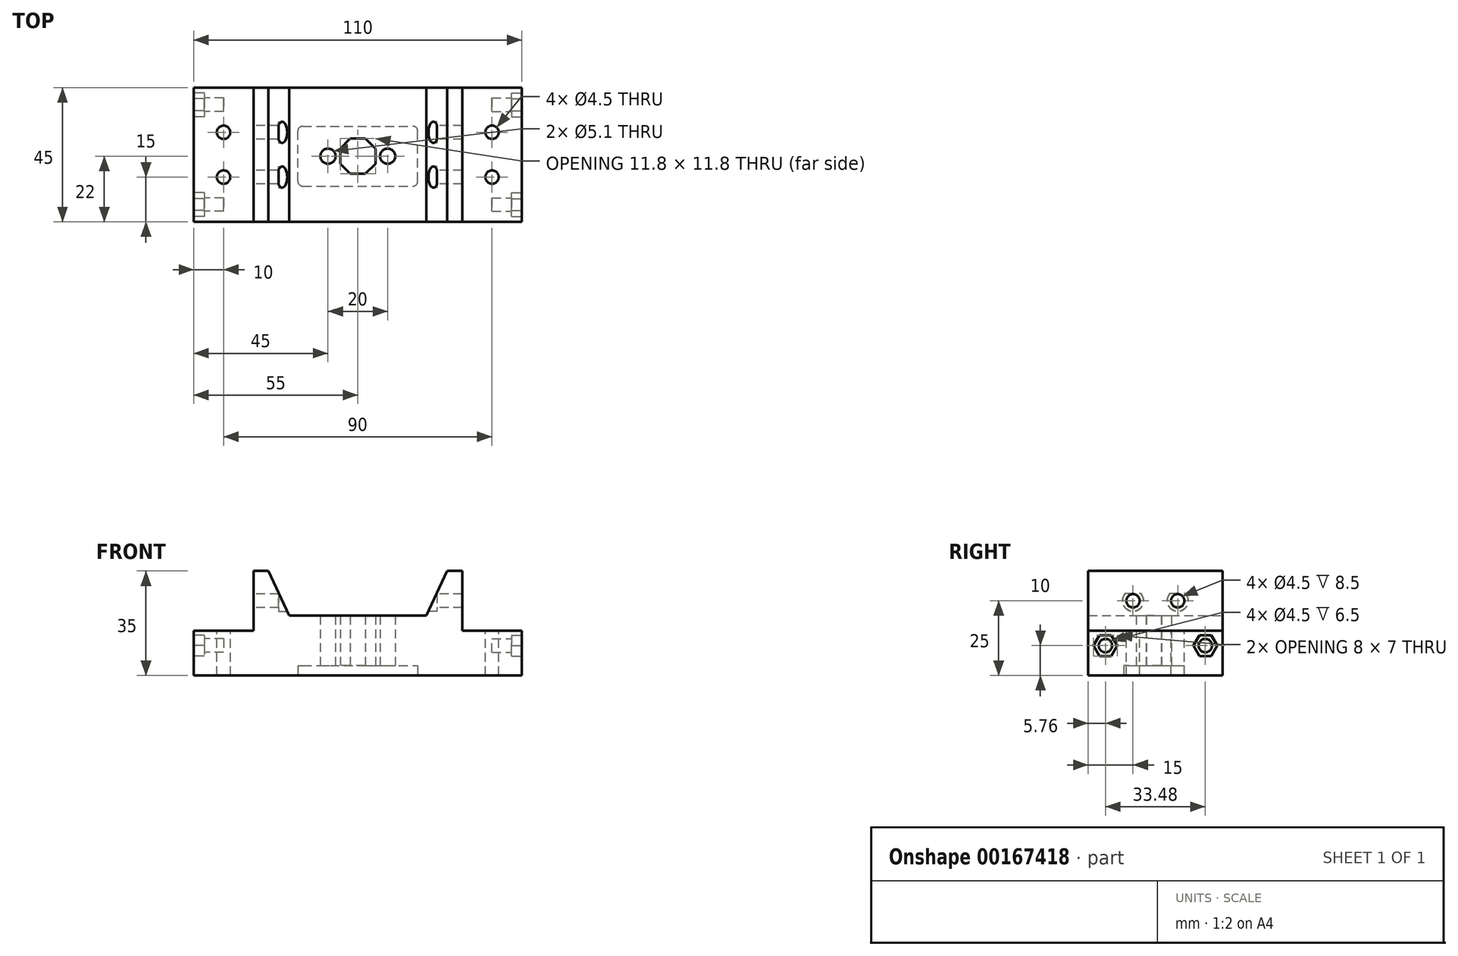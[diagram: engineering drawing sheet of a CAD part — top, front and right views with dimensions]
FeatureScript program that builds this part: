
annotation { "Feature Type Name" : "Feature", "Feature Type Description" : "" }
export const myFeature = defineFeature(function(context is Context, id is Id, definition is map)
    precondition{}
    {
        {
            var Q0;
            Q0=qCreatedBy(makeId("Top.planeOp"),FACE);
            var sketch = newSketch(context, id + "F0", { "sketchPlane" : qUnion([Q0])});
            skLineSegment(sketch, "E0", {"start": v(0, 0) * mm, "end": v(110, 0) * mm});
            skLineSegment(sketch, "E1", {"start": v(110, 0) * mm, "end": v(110, 45) * mm});
            skLineSegment(sketch, "E2", {"start": v(110, 45) * mm, "end": v(0, 45) * mm});
            skLineSegment(sketch, "E3", {"start": v(0, 45) * mm, "end": v(0, 0) * mm});
            skSolve(sketch);
        }
        {
            var Q0;
            Q0 = qSketchRegion(id + "F0", true);
            extrude(context, id + "F1", {"entities" : qUnion([Q0]), "depth" : 15 * mm});
        }
        {
            var Q0;
            Q0=makeQuery(id+"F1.opExtrude","CAP_FACE",FACE,{"disambiguationData":[OSD([sQuery(id+"F0.wireOp",EDGE,"E0"),sQuery(id+"F0.wireOp",EDGE,"E1"),sQuery(id+"F0.wireOp",EDGE,"E2"),sQuery(id+"F0.wireOp",EDGE,"E3")])],"isStart":false});
            var sketch = newSketch(context, id + "F2", { "sketchPlane" : qUnion([Q0])});
            skLineSegment(sketch, "E4", {"start": v(0, 22.5) * mm, "end": v(20, 22.5) * mm, "construction": true});
            skLineSegment(sketch, "E5", {"start": v(110, 22.5) * mm, "end": v(90, 22.5) * mm, "construction": true});
            skLineSegment(sketch, "E6", {"start": v(20, 45) * mm, "end": v(20, 0) * mm});
            skLineSegment(sketch, "E7", {"start": v(20, 0) * mm, "end": v(32, 0) * mm});
            skLineSegment(sketch, "E8", {"start": v(32, 0) * mm, "end": v(32, 45) * mm});
            skLineSegment(sketch, "E9", {"start": v(32, 45) * mm, "end": v(20, 45) * mm});
            skLineSegment(sketch, "E10", {"start": v(90, 45) * mm, "end": v(90, 0) * mm});
            skLineSegment(sketch, "E11", {"start": v(90, 0) * mm, "end": v(78, 0) * mm});
            skLineSegment(sketch, "E12", {"start": v(78, 0) * mm, "end": v(78, 45) * mm});
            skLineSegment(sketch, "E13", {"start": v(78, 45) * mm, "end": v(90, 45) * mm});
            skSolve(sketch);
        }
        {
            var Q0;
            Q0 = qSketchRegion(id + "F2", true);
            extrude(context, id + "F3", {"entities" : qUnion([Q0]), "operationType" : NewBodyOperationType.ADD, "depth" : 20 * mm});
        }
        {
            var Q0;
            Q0=qCreatedBy(makeId("Right.planeOp"),FACE);
            var sketch = newSketch(context, id + "F4", { "sketchPlane" : qUnion([Q0])});
            skCircle(sketch, "E14", {"center": v(15, 25) * mm, "radius": 2.25 * mm});
            skCircle(sketch, "E15", {"center": v(30, 25) * mm, "radius": 2.25 * mm});
            skSolve(sketch);
        }
        {
            var Q0;
            Q0 = qSketchRegion(id + "F4", true);
            var Q1;
            Q1=sQuery(id+"F4.wireOp",EDGE,"E14");
            var Q2;
            Q2=sQuery(id+"F4.wireOp",EDGE,"E15");
            extrude(context, id + "F5", {"entities" : qUnion([Q0]), "operationType" : NewBodyOperationType.REMOVE, "surfaceEntities" : qUnion([Q1, Q2]), "endBound" : BoundingType.THROUGH_ALL, "depth" : 25 * mm});
        }
        {
            var Q0;
            {var subQ0=sQuery(id+"F0.wireOp",EDGE,"E3");var subQ1=sQuery(id+"F0.wireOp",EDGE,"E2");var subQ2=sQuery(id+"F0.wireOp",EDGE,"E0");Q0=makeQuery(id+"F3.boolean.opBoolean","SPLIT",FACE,{"disambiguationData":[TD([makeQuery(id+"F1.opExtrude","SWEPT_FACE",FACE,{"disambiguationData":[OSD([subQ0])]})])],"derivedFrom":makeQuery(id+"F1.opExtrude","CAP_FACE",FACE,{"disambiguationData":[OSD([subQ2,sQuery(id+"F0.wireOp",EDGE,"E1"),subQ1,subQ0])],"isStart":false})});}
            var sketch = newSketch(context, id + "F6", { "sketchPlane" : qUnion([Q0])});
            skCircle(sketch, "E16", {"center": v(10, 30) * mm, "radius": 2.25 * mm});
            skCircle(sketch, "E17", {"center": v(10, 15) * mm, "radius": 2.25 * mm});
            skSolve(sketch);
        }
        {
            var Q0;
            Q0 = qSketchRegion(id + "F6", true);
            extrude(context, id + "F7", {"entities" : qUnion([Q0]), "operationType" : NewBodyOperationType.REMOVE, "endBound" : BoundingType.THROUGH_ALL, "oppositeDirection" : true, "depth" : 25 * mm});
        }
        {
            var Q0;
            {var subQ0=sQuery(id+"F0.wireOp",EDGE,"E2");var subQ1=sQuery(id+"F0.wireOp",EDGE,"E1");var subQ2=sQuery(id+"F0.wireOp",EDGE,"E0");Q0=makeQuery(id+"F3.boolean.opBoolean","SPLIT",FACE,{"disambiguationData":[TD([makeQuery(id+"F1.opExtrude","SWEPT_FACE",FACE,{"disambiguationData":[OSD([subQ1])]})])],"derivedFrom":makeQuery(id+"F1.opExtrude","CAP_FACE",FACE,{"disambiguationData":[OSD([subQ2,subQ1,subQ0,sQuery(id+"F0.wireOp",EDGE,"E3")])],"isStart":false})});}
            var sketch = newSketch(context, id + "F8", { "sketchPlane" : qUnion([Q0])});
            skCircle(sketch, "E18", {"center": v(100, 30) * mm, "radius": 2.25 * mm});
            skCircle(sketch, "E19", {"center": v(100, 15) * mm, "radius": 2.25 * mm});
            skSolve(sketch);
        }
        {
            var Q0;
            Q0 = qSketchRegion(id + "F8", true);
            extrude(context, id + "F9", {"entities" : qUnion([Q0]), "operationType" : NewBodyOperationType.REMOVE, "endBound" : BoundingType.THROUGH_ALL, "oppositeDirection" : true, "depth" : 25 * mm});
        }
        {
            var Q0;
            Q0=makeQuery(id+"F3.opExtrude","SWEPT_FACE",FACE,{"disambiguationData":[OSD([sQuery(id+"F2.wireOp",EDGE,"E12")])]});
            var sketch = newSketch(context, id + "F10", { "sketchPlane" : qUnion([Q0])});
            skCircle(sketch, "E20", {"center": v(-30, 25) * mm, "radius": 3.55 * mm});
            skCircle(sketch, "E21", {"center": v(-15, 25) * mm, "radius": 3.55 * mm});
            skSolve(sketch);
        }
        {
            var Q0;
            Q0 = qSketchRegion(id + "F10", true);
            extrude(context, id + "F11", {"entities" : qUnion([Q0]), "operationType" : NewBodyOperationType.REMOVE, "oppositeDirection" : true, "depth" : 3.5 * mm});
        }
        {
            var Q0;
            Q0=makeQuery(id+"F3.opExtrude","SWEPT_FACE",FACE,{"disambiguationData":[OSD([sQuery(id+"F2.wireOp",EDGE,"E8")])]});
            var sketch = newSketch(context, id + "F12", { "sketchPlane" : qUnion([Q0])});
            skCircle(sketch, "E22", {"center": v(15, 25) * mm, "radius": 3.55 * mm});
            skCircle(sketch, "E23", {"center": v(30, 25) * mm, "radius": 3.55 * mm});
            skSolve(sketch);
        }
        {
            var Q0;
            Q0 = qSketchRegion(id + "F12", true);
            extrude(context, id + "F13", {"entities" : qUnion([Q0]), "operationType" : NewBodyOperationType.REMOVE, "oppositeDirection" : true, "depth" : 3.5 * mm});
        }
        {
            var Q0;
            {var subQ0=sQuery(id+"F0.wireOp",EDGE,"E2");var subQ1=sQuery(id+"F0.wireOp",EDGE,"E0");Q0=makeQuery(id+"F3.boolean.opBoolean","SPLIT",FACE,{"disambiguationData":[TD([makeQuery(id+"F3.opExtrude","SWEPT_FACE",FACE,{"disambiguationData":[OSD([sQuery(id+"F2.wireOp",EDGE,"E8")])]})])],"derivedFrom":makeQuery(id+"F1.opExtrude","CAP_FACE",FACE,{"disambiguationData":[OSD([subQ1,sQuery(id+"F0.wireOp",EDGE,"E1"),subQ0,sQuery(id+"F0.wireOp",EDGE,"E3")])],"isStart":false})});}
            extrude(context, id + "F14", {"entities" : qUnion([Q0]), "operationType" : NewBodyOperationType.ADD, "depth" : 5 * mm});
        }
        {
            var Q0;
            {var subQ0=sQuery(id+"F0.wireOp",EDGE,"E0");Q0=makeQuery(id+"F14.boolean.opBoolean","MERGE",FACE,{"derivedFrom":[makeQuery(id+"F3.boolean.opBoolean","MERGE",FACE,{"derivedFrom":[makeQuery(id+"F1.opExtrude","SWEPT_FACE",FACE,{"disambiguationData":[OSD([subQ0])]}),makeQuery(id+"F3.opExtrude","SWEPT_FACE",FACE,{"disambiguationData":[OSD([sQuery(id+"F2.wireOp",EDGE,"E7")])]}),makeQuery(id+"F3.opExtrude","SWEPT_FACE",FACE,{"disambiguationData":[OSD([sQuery(id+"F2.wireOp",EDGE,"E11")])]})]}),makeQuery(id+"F14.opExtrude","SWEPT_FACE",FACE,{"disambiguationData":[OSD([subQ0])]})]});}
            var sketch = newSketch(context, id + "F15", { "sketchPlane" : qUnion([Q0])});
            skLineSegment(sketch, "E24", {"start": v(32, 35) * mm, "end": v(25, 35) * mm});
            skLineSegment(sketch, "E25", {"start": v(25, 35) * mm, "end": v(32, 20) * mm});
            skLineSegment(sketch, "E26", {"start": v(32, 20) * mm, "end": v(32, 35) * mm});
            skLineSegment(sketch, "E27", {"start": v(78, 35) * mm, "end": v(85, 35) * mm});
            skLineSegment(sketch, "E28", {"start": v(85, 35) * mm, "end": v(78, 20) * mm});
            skLineSegment(sketch, "E29", {"start": v(78, 20) * mm, "end": v(78, 35) * mm});
            skSolve(sketch);
        }
        {
            var Q0;
            Q0 = qSketchRegion(id + "F15", true);
            extrude(context, id + "F16", {"entities" : qUnion([Q0]), "operationType" : NewBodyOperationType.REMOVE, "endBound" : BoundingType.THROUGH_ALL, "oppositeDirection" : true, "depth" : 25 * mm});
        }
        {
            var Q0;
            Q0=makeQuery(id+"F1.opExtrude","CAP_FACE",FACE,{"disambiguationData":[OSD([sQuery(id+"F0.wireOp",EDGE,"E0"),sQuery(id+"F0.wireOp",EDGE,"E1"),sQuery(id+"F0.wireOp",EDGE,"E2"),sQuery(id+"F0.wireOp",EDGE,"E3")])],"isStart":true});
            var sketch = newSketch(context, id + "F17", { "sketchPlane" : qUnion([Q0])});
            skLineSegment(sketch, "E30", {"start": v(110, -22) * mm, "end": v(0, -22) * mm, "construction": true});
            skLineSegment(sketch, "E31", {"start": v(55, -22) * mm, "end": v(55, -16.1) * mm, "construction": true});
            skLineSegment(sketch, "E32", {"start": v(55, -22) * mm, "end": v(55, -27.9) * mm, "construction": true});
            skLineSegment(sketch, "E33", {"start": v(55, -16.1) * mm, "end": v(52.5, -16.1) * mm});
            skLineSegment(sketch, "E34", {"start": v(55, -16.1) * mm, "end": v(57.5, -16.1) * mm});
            skLineSegment(sketch, "E35", {"start": v(49.1, -22) * mm, "end": v(49.1, -24.5) * mm});
            skLineSegment(sketch, "E36", {"start": v(49.1, -22) * mm, "end": v(49.1, -19.5) * mm});
            skLineSegment(sketch, "E37", {"start": v(55, -27.9) * mm, "end": v(52.5, -27.9) * mm});
            skLineSegment(sketch, "E38", {"start": v(55, -27.9) * mm, "end": v(57.5, -27.9) * mm});
            skLineSegment(sketch, "E39", {"start": v(60.9, -22) * mm, "end": v(60.9, -19.5) * mm});
            skLineSegment(sketch, "E40", {"start": v(60.9, -22) * mm, "end": v(60.9, -24.5) * mm});
            skLineSegment(sketch, "E41", {"start": v(49.1, -19.5) * mm, "end": v(52.5, -16.1) * mm});
            skLineSegment(sketch, "E42", {"start": v(57.5, -16.1) * mm, "end": v(60.9, -19.5) * mm});
            skLineSegment(sketch, "E43", {"start": v(60.9, -24.5) * mm, "end": v(57.5, -27.9) * mm});
            skLineSegment(sketch, "E44", {"start": v(52.5, -27.9) * mm, "end": v(49.1, -24.5) * mm});
            skCircle(sketch, "E45", {"center": v(45, -22) * mm, "radius": 2.55 * mm});
            skCircle(sketch, "E46", {"center": v(65, -22) * mm, "radius": 2.55 * mm});
            skSolve(sketch);
        }
        {
            var Q0;
            Q0 = qSketchRegion(id + "F17", true);
            extrude(context, id + "F18", {"entities" : qUnion([Q0]), "operationType" : NewBodyOperationType.REMOVE, "endBound" : BoundingType.THROUGH_ALL, "oppositeDirection" : true, "depth" : 25 * mm});
        }
        {
            var Q0;
            Q0=makeQuery(id+"F1.opExtrude","CAP_FACE",FACE,{"disambiguationData":[OSD([sQuery(id+"F0.wireOp",EDGE,"E0"),sQuery(id+"F0.wireOp",EDGE,"E1"),sQuery(id+"F0.wireOp",EDGE,"E2"),sQuery(id+"F0.wireOp",EDGE,"E3")])],"isStart":true});
            var sketch = newSketch(context, id + "F19", { "sketchPlane" : qUnion([Q0])});
            skLineSegment(sketch, "E47", {"start": v(0, -22) * mm, "end": v(110, -22) * mm, "construction": true});
            skLineSegment(sketch, "E48", {"start": v(55, -22) * mm, "end": v(55, -11.95) * mm, "construction": true});
            skLineSegment(sketch, "E49", {"start": v(55, -11.95) * mm, "end": v(36.55, -11.95) * mm});
            skLineSegment(sketch, "E50", {"start": v(34.9, -13.6) * mm, "end": v(34.9, -30.4) * mm});
            skLineSegment(sketch, "E51", {"start": v(36.55, -32.05) * mm, "end": v(73.45, -32.05) * mm});
            skLineSegment(sketch, "E52", {"start": v(55, -11.95) * mm, "end": v(73.45, -11.95) * mm});
            skLineSegment(sketch, "E53", {"start": v(75.1, -13.6) * mm, "end": v(75.1, -30.4) * mm});
            skPoint(sketch, "E54.visualSharp", {"position": v(34.9, -11.95) * mm});
            skArc(sketch, "E54.filletArc", {"start": v(36.55, -11.95) * mm, "mid": v(35.38, -12.43) * mm, "end": v(34.9, -13.6) * mm});
            skPoint(sketch, "E55.visualSharp", {"position": v(34.9, -32.05) * mm});
            skArc(sketch, "E55.filletArc", {"start": v(34.9, -30.4) * mm, "mid": v(35.38, -31.57) * mm, "end": v(36.55, -32.05) * mm});
            skPoint(sketch, "E56.visualSharp", {"position": v(75.1, -32.05) * mm});
            skArc(sketch, "E56.filletArc", {"start": v(73.45, -32.05) * mm, "mid": v(74.62, -31.57) * mm, "end": v(75.1, -30.4) * mm});
            skPoint(sketch, "E57.visualSharp", {"position": v(75.1, -11.95) * mm});
            skArc(sketch, "E57.filletArc", {"start": v(75.1, -13.6) * mm, "mid": v(74.62, -12.43) * mm, "end": v(73.45, -11.95) * mm});
            skSolve(sketch);
        }
        {
            var Q0;
            Q0 = qSketchRegion(id + "F19", true);
            extrude(context, id + "F20", {"entities" : qUnion([Q0]), "operationType" : NewBodyOperationType.REMOVE, "oppositeDirection" : true, "depth" : 3.3 * mm});
        }
        {
            var Q0;
            Q0=makeQuery(id+"F1.opExtrude","SWEPT_FACE",FACE,{"disambiguationData":[OSD([sQuery(id+"F0.wireOp",EDGE,"E3")])]});
            var sketch = newSketch(context, id + "F21", { "sketchPlane" : qUnion([Q0])});
            skCircle(sketch, "E58", {"center": v(-39.24, 10) * mm, "radius": 2.25 * mm});
            skCircle(sketch, "E59", {"center": v(-5.76, 10) * mm, "radius": 2.25 * mm});
            skSolve(sketch);
        }
        {
            var Q0;
            Q0 = qSketchRegion(id + "F21", true);
            extrude(context, id + "F22", {"entities" : qUnion([Q0]), "operationType" : NewBodyOperationType.REMOVE, "oppositeDirection" : true, "depth" : 10 * mm});
        }
        {
            var Q0;
            Q0=makeQuery(id+"F1.opExtrude","SWEPT_FACE",FACE,{"disambiguationData":[OSD([sQuery(id+"F0.wireOp",EDGE,"E3")])]});
            var sketch = newSketch(context, id + "F23", { "sketchPlane" : qUnion([Q0])});
            skLineSegment(sketch, "E60", {"start": v(-39.24, 10) * mm, "end": v(-39.24, 13.5) * mm, "construction": true});
            skLineSegment(sketch, "E61", {"start": v(-39.24, 13.5) * mm, "end": v(-37.24, 13.5) * mm});
            skLineSegment(sketch, "E62", {"start": v(-39.24, 10) * mm, "end": v(-39.24, 6.5) * mm, "construction": true});
            skLineSegment(sketch, "E63", {"start": v(-39.24, 10) * mm, "end": v(-43.24, 10) * mm, "construction": true});
            skLineSegment(sketch, "E64", {"start": v(-39.24, 10) * mm, "end": v(-35.24, 10) * mm, "construction": true});
            skLineSegment(sketch, "E65", {"start": v(-39.24, 13.5) * mm, "end": v(-41.24, 13.5) * mm});
            skLineSegment(sketch, "E66", {"start": v(-39.24, 6.5) * mm, "end": v(-37.24, 6.5) * mm});
            skLineSegment(sketch, "E67", {"start": v(-39.24, 6.5) * mm, "end": v(-41.24, 6.5) * mm});
            skLineSegment(sketch, "E68", {"start": v(-43.24, 10) * mm, "end": v(-41.24, 13.5) * mm});
            skLineSegment(sketch, "E69", {"start": v(-37.24, 13.5) * mm, "end": v(-35.24, 10) * mm});
            skLineSegment(sketch, "E70", {"start": v(-37.24, 6.5) * mm, "end": v(-35.24, 10) * mm});
            skLineSegment(sketch, "E71", {"start": v(-43.24, 10) * mm, "end": v(-41.24, 6.5) * mm});
            skLineSegment(sketch, "E72", {"start": v(-5.76, 10) * mm, "end": v(-5.76, 13.5) * mm, "construction": true});
            skLineSegment(sketch, "E73", {"start": v(-5.76, 10) * mm, "end": v(-5.76, 6.5) * mm, "construction": true});
            skLineSegment(sketch, "E74", {"start": v(-5.76, 10) * mm, "end": v(-9.76, 10) * mm, "construction": true});
            skLineSegment(sketch, "E75", {"start": v(-5.76, 10) * mm, "end": v(-1.76, 10) * mm, "construction": true});
            skLineSegment(sketch, "E76", {"start": v(-5.76, 13.5) * mm, "end": v(-3.76, 13.5) * mm});
            skLineSegment(sketch, "E77", {"start": v(-5.76, 13.5) * mm, "end": v(-7.76, 13.5) * mm});
            skLineSegment(sketch, "E78", {"start": v(-5.76, 6.5) * mm, "end": v(-3.76, 6.5) * mm});
            skLineSegment(sketch, "E79", {"start": v(-5.76, 6.5) * mm, "end": v(-7.76, 6.5) * mm});
            skLineSegment(sketch, "E80", {"start": v(-9.76, 10) * mm, "end": v(-7.76, 13.5) * mm});
            skLineSegment(sketch, "E81", {"start": v(-3.76, 13.5) * mm, "end": v(-1.76, 10) * mm});
            skLineSegment(sketch, "E82", {"start": v(-3.76, 6.5) * mm, "end": v(-1.76, 10) * mm});
            skLineSegment(sketch, "E83", {"start": v(-7.76, 6.5) * mm, "end": v(-9.76, 10) * mm});
            skSolve(sketch);
        }
        {
            var Q0;
            Q0 = qSketchRegion(id + "F23", true);
            extrude(context, id + "F24", {"entities" : qUnion([Q0]), "operationType" : NewBodyOperationType.REMOVE, "oppositeDirection" : true, "depth" : 3.5 * mm});
        }
        {
            var Q0;
            Q0=makeQuery(id+"F1.opExtrude","SWEPT_FACE",FACE,{"disambiguationData":[OSD([sQuery(id+"F0.wireOp",EDGE,"E1")])]});
            var sketch = newSketch(context, id + "F25", { "sketchPlane" : qUnion([Q0])});
            skCircle(sketch, "E84", {"center": v(5.76, 10) * mm, "radius": 2.25 * mm});
            skCircle(sketch, "E85", {"center": v(39.24, 10) * mm, "radius": 2.25 * mm});
            skSolve(sketch);
        }
        {
            var Q0;
            Q0 = qSketchRegion(id + "F25", true);
            extrude(context, id + "F26", {"entities" : qUnion([Q0]), "operationType" : NewBodyOperationType.REMOVE, "oppositeDirection" : true, "depth" : 10 * mm});
        }
        {
            var Q0;
            Q0=makeQuery(id+"F1.opExtrude","SWEPT_FACE",FACE,{"disambiguationData":[OSD([sQuery(id+"F0.wireOp",EDGE,"E1")])]});
            var sketch = newSketch(context, id + "F27", { "sketchPlane" : qUnion([Q0])});
            skLineSegment(sketch, "E86", {"start": v(5.76, 10) * mm, "end": v(5.76, 13.5) * mm, "construction": true});
            skLineSegment(sketch, "E87", {"start": v(9.76, 10) * mm, "end": v(5.76, 10) * mm, "construction": true});
            skLineSegment(sketch, "E88", {"start": v(5.76, 10) * mm, "end": v(5.76, 6.5) * mm, "construction": true});
            skLineSegment(sketch, "E89", {"start": v(5.76, 10) * mm, "end": v(1.76, 10) * mm, "construction": true});
            skLineSegment(sketch, "E90", {"start": v(39.24, 10) * mm, "end": v(39.24, 13.5) * mm, "construction": true});
            skLineSegment(sketch, "E91", {"start": v(39.24, 10) * mm, "end": v(35.24, 10) * mm, "construction": true});
            skLineSegment(sketch, "E92", {"start": v(39.24, 10) * mm, "end": v(39.24, 6.5) * mm, "construction": true});
            skLineSegment(sketch, "E93", {"start": v(43.24, 10) * mm, "end": v(39.24, 10) * mm, "construction": true});
            skLineSegment(sketch, "E94", {"start": v(5.76, 13.5) * mm, "end": v(7.76, 13.5) * mm});
            skLineSegment(sketch, "E95", {"start": v(5.76, 13.5) * mm, "end": v(3.76, 13.5) * mm});
            skLineSegment(sketch, "E96", {"start": v(5.76, 6.5) * mm, "end": v(7.76, 6.5) * mm});
            skLineSegment(sketch, "E97", {"start": v(5.76, 6.5) * mm, "end": v(3.76, 6.5) * mm});
            skLineSegment(sketch, "E98", {"start": v(39.24, 6.5) * mm, "end": v(41.24, 6.5) * mm});
            skLineSegment(sketch, "E99", {"start": v(39.24, 6.5) * mm, "end": v(37.24, 6.5) * mm});
            skLineSegment(sketch, "E100", {"start": v(39.24, 13.5) * mm, "end": v(37.24, 13.5) * mm});
            skLineSegment(sketch, "E101", {"start": v(39.24, 13.5) * mm, "end": v(41.24, 13.5) * mm});
            skLineSegment(sketch, "E102", {"start": v(1.76, 10) * mm, "end": v(3.76, 13.5) * mm});
            skLineSegment(sketch, "E103", {"start": v(7.76, 13.5) * mm, "end": v(9.76, 10) * mm});
            skLineSegment(sketch, "E104", {"start": v(7.76, 6.5) * mm, "end": v(9.76, 10) * mm});
            skLineSegment(sketch, "E105", {"start": v(3.76, 6.5) * mm, "end": v(1.76, 10) * mm});
            skLineSegment(sketch, "E106", {"start": v(37.24, 13.5) * mm, "end": v(35.24, 10) * mm});
            skLineSegment(sketch, "E107", {"start": v(37.24, 6.5) * mm, "end": v(35.24, 10) * mm});
            skLineSegment(sketch, "E108", {"start": v(41.24, 6.5) * mm, "end": v(43.24, 10) * mm});
            skLineSegment(sketch, "E109", {"start": v(43.24, 10) * mm, "end": v(41.24, 13.5) * mm});
            skSolve(sketch);
        }
        {
            var Q0;
            Q0 = qSketchRegion(id + "F27", true);
            var Q1;
            Q1 = qSketchRegion(id + "F25", true);
            extrude(context, id + "F28", {"entities" : qUnion([Q0, Q1]), "operationType" : NewBodyOperationType.REMOVE, "oppositeDirection" : true, "depth" : 3.5 * mm});
        }
    });
